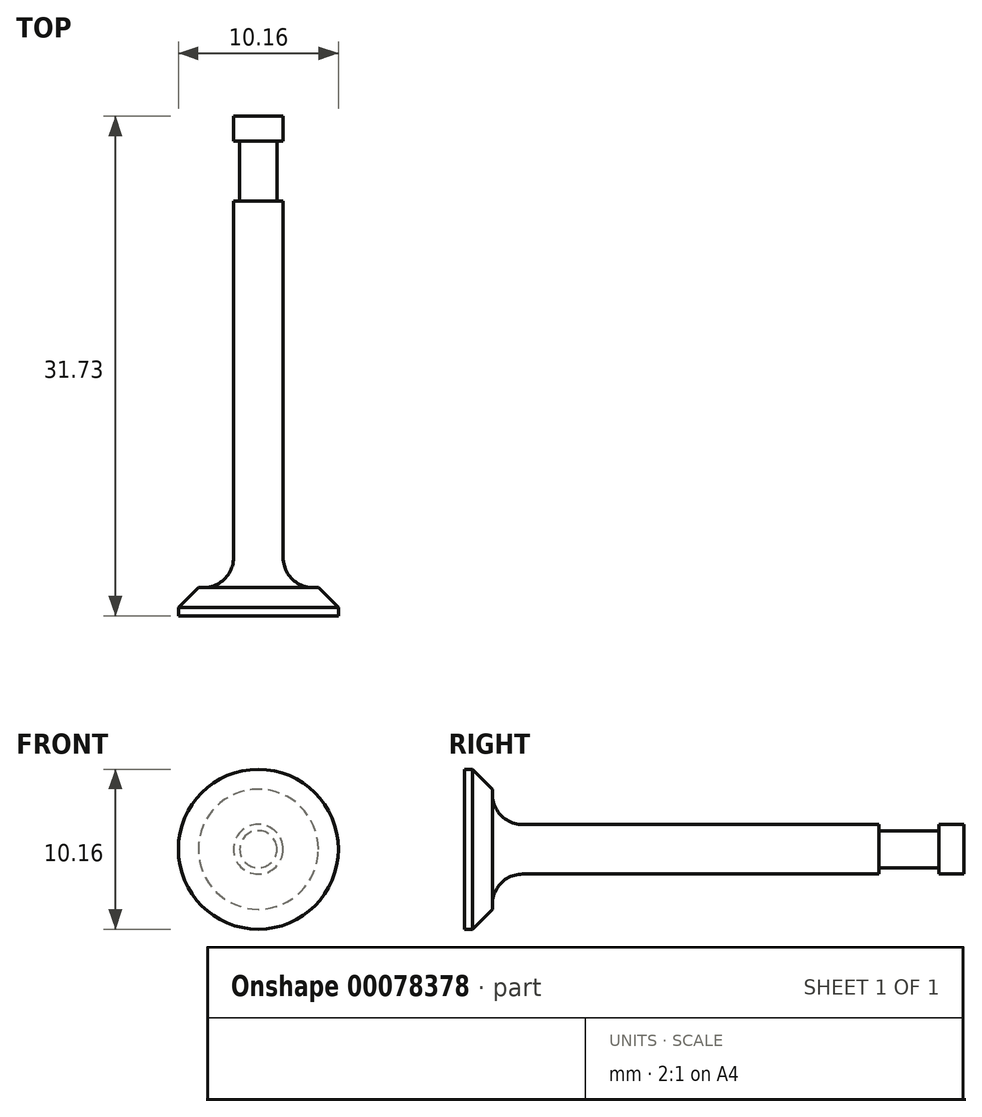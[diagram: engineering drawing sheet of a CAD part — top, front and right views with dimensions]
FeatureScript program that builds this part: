
annotation { "Feature Type Name" : "Feature", "Feature Type Description" : "" }
export const myFeature = defineFeature(function(context is Context, id is Id, definition is map)
    precondition{}
    {
        {
            var Q0;
            Q0=qCreatedBy(makeId("Right.planeOp"),FACE);
            var sketch = newSketch(context, id + "F0", { "sketchPlane" : qUnion([Q0])});
            skLineSegment(sketch, "E0", {"start": v(1.66, 5.08) * mm, "end": v(2.93, 3.81) * mm});
            skPoint(sketch, "E1.orphan", {"position": v(2.93, 0) * mm});
            skLineSegment(sketch, "E2", {"start": v(4.83, 1.58) * mm, "end": v(27.49, 1.58) * mm});
            skLineSegment(sketch, "E3", {"start": v(27.49, 1.58) * mm, "end": v(27.49, 1.18) * mm});
            skLineSegment(sketch, "E4", {"start": v(2.93, 3.81) * mm, "end": v(2.93, 3.48) * mm});
            skPoint(sketch, "E5.visualSharp", {"position": v(2.93, 1.58) * mm});
            skArc(sketch, "E5.filletArc", {"start": v(2.93, 3.48) * mm, "mid": v(3.49, 2.14) * mm, "end": v(4.83, 1.58) * mm});
            skLineSegment(sketch, "E6", {"start": v(27.49, 1.18) * mm, "end": v(31.3, 1.18) * mm});
            skLineSegment(sketch, "E7", {"start": v(31.3, 1.18) * mm, "end": v(31.3, 1.58) * mm});
            skLineSegment(sketch, "E8", {"start": v(31.3, 1.58) * mm, "end": v(32.87, 1.58) * mm});
            skLineSegment(sketch, "E9", {"start": v(32.87, 1.58) * mm, "end": v(32.87, 0) * mm});
            skLineSegment(sketch, "E10", {"start": v(32.87, 0) * mm, "end": v(1.14, 0) * mm});
            skLineSegment(sketch, "E11", {"start": v(1.14, 5.08) * mm, "end": v(1.66, 5.08) * mm});
            skLineSegment(sketch, "E12", {"start": v(1.14, 5.08) * mm, "end": v(1.14, 0) * mm});
            skSolve(sketch);
        }
        {
            var Q0;
            Q0=makeQuery(id+"F0.imprint","IMPRINT",FACE,{"disambiguationData":[TD([[makeQuery(id+"F0.imprint","IMPRINT",EDGE,{"derivedFrom":sQuery(id+"F0.wireOp",EDGE,"E0")}),-1.0]])]});
            var Q1;
            Q1=sQuery(id+"F0.wireOp",EDGE,"E10");
            revolve(context, id + "F1", {"entities" : qUnion([Q0]), "axis" : qUnion([Q1]), "revolveType" : RevolveType.FULL});
        }
    });
